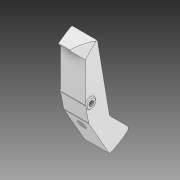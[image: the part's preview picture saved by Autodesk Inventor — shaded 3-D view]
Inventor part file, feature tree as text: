
AUTODESK INVENTOR PART (.ipt)
format: ipt  version: 2020 (Build 240168000, 168)  size: 214,016 bytes
history: native  units: in
note: dims shown in document units (in); Inventor stores cm internally (conversion verified against a paired STEP export)
features: extrude x5, sketch x5, chamfer x2, projected_geometry x1, imported_body x1
ambient origin geometry x8: Origin, YZ Plane, XZ Plane, XY Plane, X Axis, Y Axis, Z Axis, Center Point
bodies: Solid1 (feature_tree)
feature tree (14):
  extrude  "Extrusion1"  Depth=0.1969in
  extrude  "Extrusion2"  Depth=0.1575in
  extrude  "Extrusion3"  Depth=0.0197in TaperAngle=45.0deg
  chamfer  "Chamfer1"  Distance=0.0197in
  extrude  "Extrusion4"  Depth=0.1496in
  chamfer  "Chamfer2"  Distance=0.5512in
  extrude  "Extrusion5"  TaperAngle=0.0deg  [1 undecoded]
  sketch  "Sketch1"  dims[d0=0.4528in d1=0.0in d2=0.1969in]
  projected_geometry  "Projected Loop1"
  sketch  "Sketch2"  dims[d3=0.4528in d4=0.0in d5=0.1575in]
  sketch  "Sketch3"  dims[d6=0.0197in d7=0.0in d8=0.0197in d9=0.0787in d10=45.0deg]
  sketch  "Sketch4"  dims[d11=0.1575in d12=0.0197in d13=0.0in]
  sketch  "Sketch5"  dims[d14=0.0197in d15=0.0787in d16=45.0deg d17=0.1496in d18=0.5512in d19=0.0in d20=0.0in]
  imported_body  "Base1"
note: 1 required parameter value undecoded (feature->parameter linkage not recoverable at this tier; creation-order binding heuristic only, values carry confidence <= 0.55)
